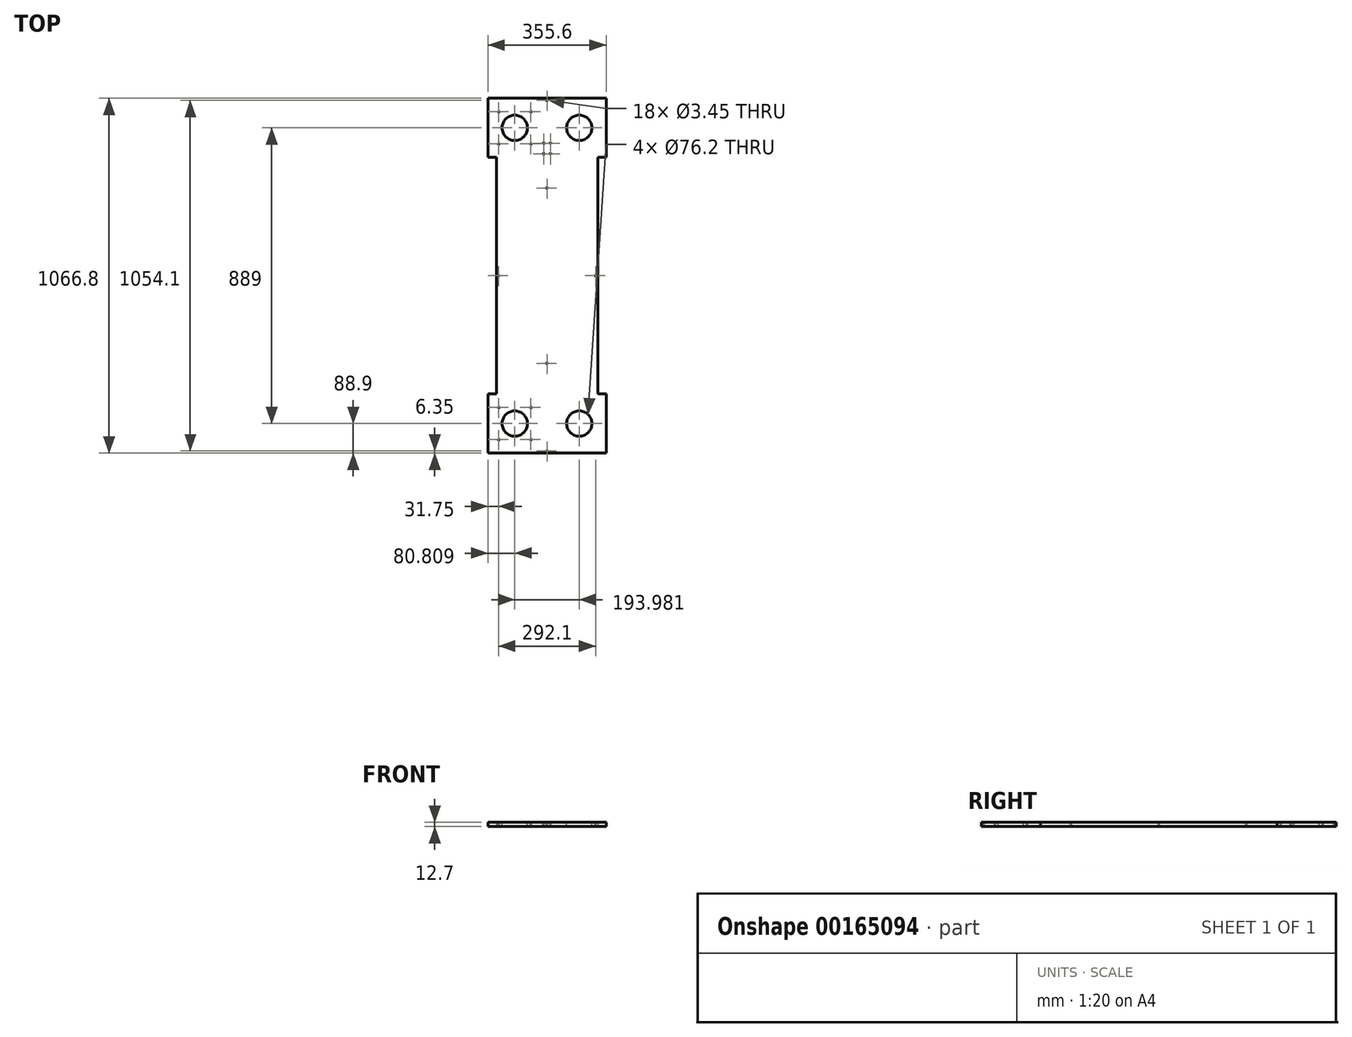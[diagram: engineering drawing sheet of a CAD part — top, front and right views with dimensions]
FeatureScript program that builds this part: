
annotation { "Feature Type Name" : "Feature", "Feature Type Description" : "" }
export const myFeature = defineFeature(function(context is Context, id is Id, definition is map)
    precondition{}
    {
        {
            var Q0;
            Q0=qCreatedBy(makeId("Top.planeOp"),FACE);
            var sketch = newSketch(context, id + "F0", { "sketchPlane" : qUnion([Q0])});
            skLineSegment(sketch, "E0", {"start": v(-152.4, 0) * mm, "end": v(152.4, 0) * mm, "construction": true});
            skLineSegment(sketch, "E1.left", {"start": v(-152.4, -355.6) * mm, "end": v(-152.4, 355.6) * mm});
            skLineSegment(sketch, "E1.right", {"start": v(152.4, -355.6) * mm, "end": v(152.4, 355.6) * mm});
            skLineSegment(sketch, "E2.bottom", {"start": v(-152.4, 355.6) * mm, "end": v(-177.8, 355.6) * mm});
            skLineSegment(sketch, "E2.top", {"start": v(177.8, 533.4) * mm, "end": v(-177.8, 533.4) * mm});
            skLineSegment(sketch, "E2.left", {"start": v(177.8, 355.6) * mm, "end": v(177.8, 533.4) * mm});
            skLineSegment(sketch, "E2.right", {"start": v(-177.8, 355.6) * mm, "end": v(-177.8, 533.4) * mm});
            skLineSegment(sketch, "E3", {"start": v(0, 0) * mm, "end": v(0, 533.4) * mm, "construction": true});
            skLineSegment(sketch, "E4", {"start": v(152.4, 355.6) * mm, "end": v(177.8, 355.6) * mm});
            skLineSegment(sketch, "E5", {"start": v(0, 0) * mm, "end": v(0, -533.4) * mm, "construction": true});
            skPoint(sketch, "E6.middle", {"position": v(0, 0) * mm});
            skLineSegment(sketch, "E7", {"start": v(-177.8, 444.5) * mm, "end": v(0, 444.5) * mm, "construction": true});
            skLineSegment(sketch, "E8", {"start": v(-152.4, -355.6) * mm, "end": v(-177.8, -355.6) * mm});
            skLineSegment(sketch, "E9", {"start": v(-177.8, -355.6) * mm, "end": v(-177.8, -533.4) * mm});
            skLineSegment(sketch, "E10", {"start": v(-177.8, -533.4) * mm, "end": v(177.8, -533.4) * mm});
            skLineSegment(sketch, "E11", {"start": v(177.8, -533.4) * mm, "end": v(177.8, -355.6) * mm});
            skLineSegment(sketch, "E12", {"start": v(177.8, -355.6) * mm, "end": v(152.4, -355.6) * mm});
            skSolve(sketch);
        }
        {
            var Q0;
            Q0=qSketchRegion(id+"F0",true);
            extrude(context, id + "F1", {"entities" : qUnion([Q0]), "depth" : 12.7 * mm});
        }
        {
            var Q0;
            Q0=makeQuery(id+"F1.opExtrude","CAP_FACE",FACE,{"disambiguationData":[OSD([sQuery(id+"F0.wireOp",EDGE,"E1.left"),sQuery(id+"F0.wireOp",EDGE,"E1.right"),sQuery(id+"F0.wireOp",EDGE,"E2.bottom"),sQuery(id+"F0.wireOp",EDGE,"E2.top"),sQuery(id+"F0.wireOp",EDGE,"E2.left"),sQuery(id+"F0.wireOp",EDGE,"E2.right"),sQuery(id+"F0.wireOp",EDGE,"E4"),sQuery(id+"F0.wireOp",EDGE,"E8"),sQuery(id+"F0.wireOp",EDGE,"E9"),sQuery(id+"F0.wireOp",EDGE,"E10"),sQuery(id+"F0.wireOp",EDGE,"E11"),sQuery(id+"F0.wireOp",EDGE,"E12")])],"isStart":false});
            var sketch = newSketch(context, id + "F2", { "sketchPlane" : qUnion([Q0])});
            skLineSegment(sketch, "E13.bottom", {"start": v(-177.8, 533.4) * mm, "end": v(-97, 533.4) * mm, "construction": true});
            skLineSegment(sketch, "E13.top", {"start": v(-177.8, 444.5) * mm, "end": v(-97, 444.5) * mm, "construction": true});
            skLineSegment(sketch, "E13.left", {"start": v(-177.8, 533.4) * mm, "end": v(-177.8, 444.5) * mm, "construction": true});
            skLineSegment(sketch, "E13.right", {"start": v(-97, 533.4) * mm, "end": v(-97, 444.5) * mm, "construction": true});
            skLineSegment(sketch, "E14.bottom", {"start": v(177.8, 533.4) * mm, "end": v(97, 533.4) * mm, "construction": true});
            skLineSegment(sketch, "E14.top", {"start": v(177.8, 444.5) * mm, "end": v(97, 444.5) * mm, "construction": true});
            skLineSegment(sketch, "E14.left", {"start": v(177.8, 533.4) * mm, "end": v(177.8, 444.5) * mm, "construction": true});
            skLineSegment(sketch, "E14.right", {"start": v(97, 533.4) * mm, "end": v(97, 444.5) * mm, "construction": true});
            skLineSegment(sketch, "E15.bottom", {"start": v(177.8, -533.4) * mm, "end": v(97, -533.4) * mm, "construction": true});
            skLineSegment(sketch, "E15.top", {"start": v(177.8, -444.5) * mm, "end": v(97, -444.5) * mm, "construction": true});
            skLineSegment(sketch, "E15.left", {"start": v(177.8, -533.4) * mm, "end": v(177.8, -444.5) * mm, "construction": true});
            skLineSegment(sketch, "E15.right", {"start": v(97, -533.4) * mm, "end": v(97, -444.5) * mm, "construction": true});
            skLineSegment(sketch, "E16.bottom", {"start": v(-177.8, -533.4) * mm, "end": v(-97, -533.4) * mm, "construction": true});
            skLineSegment(sketch, "E16.top", {"start": v(-177.8, -444.5) * mm, "end": v(-97, -444.5) * mm, "construction": true});
            skLineSegment(sketch, "E16.left", {"start": v(-177.8, -533.4) * mm, "end": v(-177.8, -444.5) * mm, "construction": true});
            skLineSegment(sketch, "E16.right", {"start": v(-97, -533.4) * mm, "end": v(-97, -444.5) * mm, "construction": true});
            skLineSegment(sketch, "E17.bottom", {"start": v(-145.37, -396.12) * mm, "end": v(-48.6, -396.12) * mm, "construction": true});
            skLineSegment(sketch, "E17.top", {"start": v(-145.37, -492.88) * mm, "end": v(-48.6, -492.88) * mm, "construction": true});
            skLineSegment(sketch, "E17.left", {"start": v(-145.37, -396.12) * mm, "end": v(-145.37, -492.88) * mm, "construction": true});
            skLineSegment(sketch, "E17.right", {"start": v(-48.6, -396.12) * mm, "end": v(-48.6, -492.88) * mm, "construction": true});
            skPoint(sketch, "E17.middle", {"position": v(-97, -444.5) * mm});
            skLineSegment(sketch, "E18.bottom", {"start": v(48.6, -396.12) * mm, "end": v(145.37, -396.12) * mm, "construction": true});
            skLineSegment(sketch, "E18.top", {"start": v(48.6, -492.88) * mm, "end": v(145.37, -492.88) * mm, "construction": true});
            skLineSegment(sketch, "E18.left", {"start": v(48.6, -396.12) * mm, "end": v(48.6, -492.88) * mm, "construction": true});
            skLineSegment(sketch, "E18.right", {"start": v(145.37, -396.12) * mm, "end": v(145.37, -492.88) * mm, "construction": true});
            skPoint(sketch, "E18.middle", {"position": v(97, -444.5) * mm});
            skLineSegment(sketch, "E19.bottom", {"start": v(48.6, 396.12) * mm, "end": v(145.37, 396.12) * mm, "construction": true});
            skLineSegment(sketch, "E19.top", {"start": v(48.6, 492.88) * mm, "end": v(145.37, 492.88) * mm, "construction": true});
            skLineSegment(sketch, "E19.left", {"start": v(48.6, 396.12) * mm, "end": v(48.6, 492.88) * mm, "construction": true});
            skLineSegment(sketch, "E19.right", {"start": v(145.37, 396.12) * mm, "end": v(145.37, 492.88) * mm, "construction": true});
            skPoint(sketch, "E19.middle", {"position": v(97, 444.5) * mm});
            skLineSegment(sketch, "E20.bottom", {"start": v(-48.6, 396.12) * mm, "end": v(-145.37, 396.12) * mm, "construction": true});
            skLineSegment(sketch, "E20.top", {"start": v(-48.6, 492.88) * mm, "end": v(-145.37, 492.88) * mm, "construction": true});
            skLineSegment(sketch, "E20.left", {"start": v(-48.6, 396.12) * mm, "end": v(-48.6, 492.88) * mm, "construction": true});
            skLineSegment(sketch, "E20.right", {"start": v(-145.37, 396.12) * mm, "end": v(-145.37, 492.88) * mm, "construction": true});
            skPoint(sketch, "E20.middle", {"position": v(-97, 444.5) * mm});
            skCircle(sketch, "E21", {"center": v(-145.37, 492.88) * mm, "radius": 1.73 * mm});
            skCircle(sketch, "E22", {"center": v(-48.6, 492.88) * mm, "radius": 1.73 * mm});
            skCircle(sketch, "E23", {"center": v(-145.37, 396.12) * mm, "radius": 1.73 * mm});
            skCircle(sketch, "E24", {"center": v(-48.6, 396.12) * mm, "radius": 1.73 * mm});
            skCircle(sketch, "E25", {"center": v(-145.37, -492.88) * mm, "radius": 1.73 * mm});
            skCircle(sketch, "E26", {"center": v(-145.37, -396.12) * mm, "radius": 1.73 * mm});
            skCircle(sketch, "E27", {"center": v(-48.6, -492.88) * mm, "radius": 1.73 * mm});
            skCircle(sketch, "E28", {"center": v(-48.6, -396.12) * mm, "radius": 1.73 * mm});
            skCircle(sketch, "E29", {"center": v(-97, -444.5) * mm, "radius": 38.1 * mm});
            skCircle(sketch, "E30", {"center": v(97, -444.5) * mm, "radius": 38.1 * mm});
            skCircle(sketch, "E31", {"center": v(-97, 444.5) * mm, "radius": 38.1 * mm});
            skCircle(sketch, "E32", {"center": v(97, 444.5) * mm, "radius": 38.1 * mm});
            skLineSegment(sketch, "E33", {"start": v(0, 382.66) * mm, "end": v(0, -382.66) * mm, "construction": true});
            skLineSegment(sketch, "E34", {"start": v(0, 0) * mm, "end": v(152.4, 0) * mm, "construction": true});
            skLineSegment(sketch, "E35", {"start": v(0, 0) * mm, "end": v(-152.4, 0) * mm, "construction": true});
            skLineSegment(sketch, "E36.bottom", {"start": v(10.32, 398.54) * mm, "end": v(-10.32, 398.54) * mm, "construction": true});
            skLineSegment(sketch, "E36.top", {"start": v(10.32, 366.79) * mm, "end": v(-10.32, 366.79) * mm, "construction": true});
            skLineSegment(sketch, "E36.left", {"start": v(10.32, 398.54) * mm, "end": v(10.32, 366.79) * mm, "construction": true});
            skLineSegment(sketch, "E36.right", {"start": v(-10.32, 398.54) * mm, "end": v(-10.32, 366.79) * mm, "construction": true});
            skPoint(sketch, "E36.middle", {"position": v(0, 382.66) * mm});
            skLineSegment(sketch, "E37.bottom", {"start": v(10.32, -398.54) * mm, "end": v(-10.32, -398.54) * mm, "construction": true});
            skLineSegment(sketch, "E37.top", {"start": v(10.32, -366.79) * mm, "end": v(-10.32, -366.79) * mm, "construction": true});
            skLineSegment(sketch, "E37.left", {"start": v(10.32, -398.54) * mm, "end": v(10.32, -366.79) * mm, "construction": true});
            skLineSegment(sketch, "E37.right", {"start": v(-10.32, -398.54) * mm, "end": v(-10.32, -366.79) * mm, "construction": true});
            skPoint(sketch, "E37.middle", {"position": v(0, -382.66) * mm});
            skCircle(sketch, "E38", {"center": v(-10.32, 366.79) * mm, "radius": 1.73 * mm});
            skCircle(sketch, "E39", {"center": v(10.32, 398.54) * mm, "radius": 1.73 * mm});
            skCircle(sketch, "E40", {"center": v(10.32, 366.79) * mm, "radius": 1.73 * mm});
            skCircle(sketch, "E41", {"center": v(-10.32, 398.54) * mm, "radius": 1.73 * mm});
            skSolve(sketch);
        }
        {
            var Q0;
            Q0 = qSketchRegion(id + "F2", true);
            var Q1;
            Q1=makeQuery(id+"F1.opExtrude","CAP_FACE",FACE,{"disambiguationData":[OSD([sQuery(id+"F0.wireOp",EDGE,"E1.left"),sQuery(id+"F0.wireOp",EDGE,"E1.right"),sQuery(id+"F0.wireOp",EDGE,"E2.bottom"),sQuery(id+"F0.wireOp",EDGE,"E2.top"),sQuery(id+"F0.wireOp",EDGE,"E2.left"),sQuery(id+"F0.wireOp",EDGE,"E2.right"),sQuery(id+"F0.wireOp",EDGE,"E4"),sQuery(id+"F0.wireOp",EDGE,"E8"),sQuery(id+"F0.wireOp",EDGE,"E9"),sQuery(id+"F0.wireOp",EDGE,"E10"),sQuery(id+"F0.wireOp",EDGE,"E11"),sQuery(id+"F0.wireOp",EDGE,"E12")])],"isStart":true});
            extrude(context, id + "F3", {"entities" : qUnion([Q0]), "operationType" : NewBodyOperationType.REMOVE, "endBound" : BoundingType.UP_TO_SURFACE, "oppositeDirection" : true, "endBoundEntityFace" : qUnion([Q1]), "depth" : 25.4 * mm});
        }
        {
            var Q0;
            Q0=makeQuery(id+"F1.opExtrude","CAP_FACE",FACE,{"disambiguationData":[OSD([sQuery(id+"F0.wireOp",EDGE,"E1.left"),sQuery(id+"F0.wireOp",EDGE,"E1.right"),sQuery(id+"F0.wireOp",EDGE,"E2.bottom"),sQuery(id+"F0.wireOp",EDGE,"E2.top"),sQuery(id+"F0.wireOp",EDGE,"E2.left"),sQuery(id+"F0.wireOp",EDGE,"E2.right"),sQuery(id+"F0.wireOp",EDGE,"E4"),sQuery(id+"F0.wireOp",EDGE,"E8"),sQuery(id+"F0.wireOp",EDGE,"E9"),sQuery(id+"F0.wireOp",EDGE,"E10"),sQuery(id+"F0.wireOp",EDGE,"E11"),sQuery(id+"F0.wireOp",EDGE,"E12")])],"isStart":false});
            var sketch = newSketch(context, id + "F4", { "sketchPlane" : qUnion([Q0])});
            skLineSegment(sketch, "E42", {"start": v(0, 533.4) * mm, "end": v(0, 527.05) * mm, "construction": true});
            skLineSegment(sketch, "E43", {"start": v(-152.4, 0) * mm, "end": v(-146.05, 0) * mm, "construction": true});
            skLineSegment(sketch, "E44", {"start": v(-146.05, 0) * mm, "end": v(146.05, 0) * mm, "construction": true});
            skLineSegment(sketch, "E45", {"start": v(146.05, 0) * mm, "end": v(152.4, 0) * mm, "construction": true});
            skLineSegment(sketch, "E46", {"start": v(0, 527.05) * mm, "end": v(0, 263.53) * mm, "construction": true});
            skLineSegment(sketch, "E47", {"start": v(0, 263.53) * mm, "end": v(0, 0) * mm, "construction": true});
            skLineSegment(sketch, "E48", {"start": v(0, 0) * mm, "end": v(0, -263.53) * mm, "construction": true});
            skLineSegment(sketch, "E49", {"start": v(0, -263.53) * mm, "end": v(0, -527.05) * mm, "construction": true});
            skLineSegment(sketch, "E50", {"start": v(0, -527.05) * mm, "end": v(0, -533.4) * mm, "construction": true});
            skCircle(sketch, "E51", {"center": v(0, 263.53) * mm, "radius": 1.73 * mm});
            skCircle(sketch, "E52", {"center": v(-146.05, 0) * mm, "radius": 1.73 * mm});
            skCircle(sketch, "E53", {"center": v(146.05, 0) * mm, "radius": 1.73 * mm});
            skCircle(sketch, "E54", {"center": v(0, 527.05) * mm, "radius": 1.73 * mm});
            skCircle(sketch, "E55", {"center": v(0, -263.53) * mm, "radius": 1.73 * mm});
            skCircle(sketch, "E56", {"center": v(0, -527.05) * mm, "radius": 1.73 * mm});
            skSolve(sketch);
        }
        {
            var Q0;
            Q0 = qSketchRegion(id + "F4", true);
            var Q1;
            Q1=makeQuery(id+"F1.opExtrude","CAP_FACE",FACE,{"disambiguationData":[OSD([sQuery(id+"F0.wireOp",EDGE,"E1.left"),sQuery(id+"F0.wireOp",EDGE,"E1.right"),sQuery(id+"F0.wireOp",EDGE,"E2.bottom"),sQuery(id+"F0.wireOp",EDGE,"E2.top"),sQuery(id+"F0.wireOp",EDGE,"E2.left"),sQuery(id+"F0.wireOp",EDGE,"E2.right"),sQuery(id+"F0.wireOp",EDGE,"E4"),sQuery(id+"F0.wireOp",EDGE,"E8"),sQuery(id+"F0.wireOp",EDGE,"E9"),sQuery(id+"F0.wireOp",EDGE,"E10"),sQuery(id+"F0.wireOp",EDGE,"E11"),sQuery(id+"F0.wireOp",EDGE,"E12")])],"isStart":true});
            extrude(context, id + "F5", {"entities" : qUnion([Q0]), "operationType" : NewBodyOperationType.REMOVE, "endBound" : BoundingType.UP_TO_SURFACE, "oppositeDirection" : true, "endBoundEntityFace" : qUnion([Q1]), "depth" : 25.4 * mm});
        }
    });
